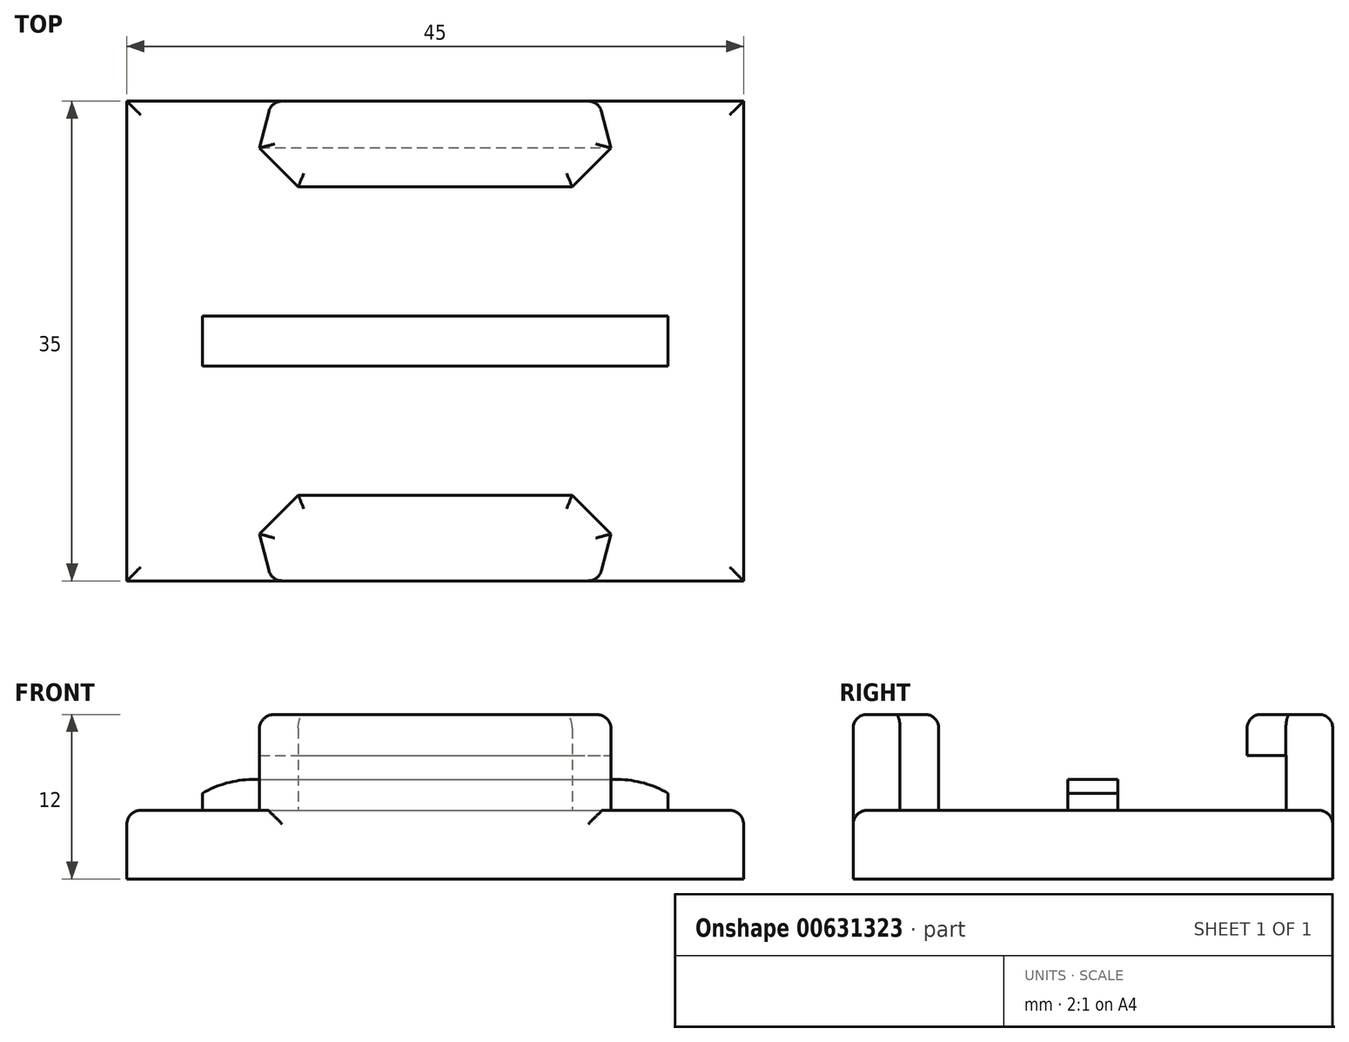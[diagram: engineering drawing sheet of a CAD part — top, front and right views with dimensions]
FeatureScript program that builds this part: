
annotation { "Feature Type Name" : "Feature", "Feature Type Description" : "" }
export const myFeature = defineFeature(function(context is Context, id is Id, definition is map)
    precondition{}
    {
        {
            var Q0;
            Q0=qCreatedBy(makeId("Top.planeOp"),FACE);
            var sketch = newSketch(context, id + "F0", { "sketchPlane" : qUnion([Q0])});
            skLineSegment(sketch, "E0.rect.bottom", {"start": v(-22.5, 17.5) * mm, "end": v(22.5, 17.5) * mm});
            skLineSegment(sketch, "E0.rect.top", {"start": v(-22.5, -17.5) * mm, "end": v(22.5, -17.5) * mm});
            skLineSegment(sketch, "E0.rect.left", {"start": v(-22.5, 17.5) * mm, "end": v(-22.5, -17.5) * mm});
            skLineSegment(sketch, "E0.rect.right", {"start": v(22.5, 17.5) * mm, "end": v(22.5, -17.5) * mm});
            skPoint(sketch, "E0.rect.middle", {"position": v(0, 0) * mm});
            skSolve(sketch);
        }
        {
            var Q0;
            Q0=makeQuery(id+"F0.imprint","IMPRINT",FACE,{"disambiguationData":[TD([[makeQuery(id+"F0.imprint","IMPRINT",EDGE,{"derivedFrom":sQuery(id+"F0.wireOp",EDGE,"E0.rect.bottom")}),-1.0]])]});
            extrude(context, id + "F1", {"entities" : qUnion([Q0]), "depth" : 5 * mm});
        }
        {
            var Q0;
            Q0=makeQuery(id+"F1.opExtrude","CAP_FACE",FACE,{"disambiguationData":[OSD([sQuery(id+"F0.wireOp",EDGE,"E0.rect.bottom"),sQuery(id+"F0.wireOp",EDGE,"E0.rect.top"),sQuery(id+"F0.wireOp",EDGE,"E0.rect.left"),sQuery(id+"F0.wireOp",EDGE,"E0.rect.right")])],"isStart":false});
            var sketch = newSketch(context, id + "F2", { "sketchPlane" : qUnion([Q0])});
            skLineSegment(sketch, "E1.rect.bottom", {"start": v(-17, 1.82) * mm, "end": v(17, 1.82) * mm});
            skLineSegment(sketch, "E1.rect.top", {"start": v(-17, -1.83) * mm, "end": v(17, -1.83) * mm});
            skLineSegment(sketch, "E1.rect.left", {"start": v(-17, 1.82) * mm, "end": v(-17, -1.83) * mm});
            skLineSegment(sketch, "E1.rect.right", {"start": v(17, 1.82) * mm, "end": v(17, -1.83) * mm});
            skPoint(sketch, "E1.rect.middle", {"position": v(0, 0) * mm});
            skSolve(sketch);
        }
        {
            var Q0;
            Q0=makeQuery(id+"F2.imprint","IMPRINT",FACE,{"disambiguationData":[TD([[makeQuery(id+"F2.imprint","IMPRINT",EDGE,{"derivedFrom":sQuery(id+"F2.wireOp",EDGE,"E1.rect.bottom")}),-1.0]])]});
            extrude(context, id + "F3", {"entities" : qUnion([Q0]), "operationType" : NewBodyOperationType.ADD, "depth" : 2.25 * mm});
        }
        {
            var Q0;
            Q0=makeQuery(id+"F3.opExtrude","SWEPT_FACE",FACE,{"disambiguationData":[OSD([sQuery(id+"F2.wireOp",EDGE,"E1.rect.top")])]});
            var sketch = newSketch(context, id + "F4", { "sketchPlane" : qUnion([Q0])});
            skLineSegment(sketch, "E2", {"start": v(-17, 7.25) * mm, "end": v(17, 7.25) * mm, "construction": true});
            skLineSegment(sketch, "E3.0", {"start": v(-17, 6.25) * mm, "end": v(17, 6.25) * mm});
            skArc(sketch, "E4", {"start": v(-13.26, 7.25) * mm, "mid": v(-15.2, 7) * mm, "end": v(-17, 6.25) * mm});
            skLineSegment(sketch, "E5", {"start": v(0, 0) * mm, "end": v(0, 15.47) * mm, "construction": true});
            skArc(sketch, "E6.0.MirrorCS", {"start": v(13.26, 7.25) * mm, "mid": v(15.2, 7) * mm, "end": v(17, 6.25) * mm});
            skLineSegment(sketch, "E7", {"start": v(-17, 6.25) * mm, "end": v(-18.16, 6.25) * mm});
            skLineSegment(sketch, "E8", {"start": v(-18.16, 6.25) * mm, "end": v(-18.16, 8.7) * mm});
            skLineSegment(sketch, "E9", {"start": v(-18.16, 8.7) * mm, "end": v(-13.25, 8.7) * mm});
            skLineSegment(sketch, "E10", {"start": v(-13.25, 8.7) * mm, "end": v(-13.26, 7.25) * mm});
            skLineSegment(sketch, "E11", {"start": v(13.26, 7.25) * mm, "end": v(13.26, 8.4) * mm});
            skLineSegment(sketch, "E12", {"start": v(13.26, 8.4) * mm, "end": v(18.11, 8.4) * mm});
            skLineSegment(sketch, "E13", {"start": v(18.11, 8.4) * mm, "end": v(18.11, 6.28) * mm});
            skLineSegment(sketch, "E14", {"start": v(18.11, 6.28) * mm, "end": v(17, 6.25) * mm});
            skSolve(sketch);
        }
        {
            var Q0;
            {var subQ0=sQuery(id+"F2.wireOp",EDGE,"E1.rect.top");var subQ1=makeQuery(id+"F3.opExtrude","CAP_EDGE",EDGE,{"disambiguationData":[OSD([subQ0])],"isStart":false});var subQ2=sQuery(id+"F4.wireOp",EDGE,"E4");var subQ3=makeQuery(id+"F4.imprint","INTERSECT",VERTEX,{"derivedFrom":[subQ1,subQ2]});var subQ6=makeQuery(id+"F4.imprint","IMPRINT",EDGE,{"disambiguationData":[TD([[subQ3,1.0]])],"derivedFrom":subQ1});var subQ8=sQuery(id+"F4.wireOp",EDGE,"E7");var subQ13=sQuery(id+"F4.wireOp",EDGE,"E6.0.MirrorCS");var subQ18=makeQuery(id+"F4.imprint","INTERSECT",VERTEX,{"derivedFrom":[subQ1,subQ13]});var subQ19=makeQuery(id+"F4.imprint","IMPRINT",EDGE,{"disambiguationData":[TD([[subQ18,-1.0]])],"derivedFrom":subQ1});var subQ20=sQuery(id+"F4.wireOp",EDGE,"E11");Q0=qUnion([makeQuery(id+"F4.imprint","IMPRINT",FACE,{"disambiguationData":[TD([[makeQuery(id+"F4.imprint","IMPRINT",EDGE,{"derivedFrom":subQ8}),-1.0]])]}),makeQuery(id+"F4.imprint","IMPRINT",FACE,{"disambiguationData":[TD([[subQ6,-1.0]])]}),makeQuery(id+"F4.imprint","IMPRINT",FACE,{"disambiguationData":[TD([[makeQuery(id+"F4.imprint","IMPRINT",EDGE,{"derivedFrom":subQ20}),-1.0]])]}),makeQuery(id+"F4.imprint","IMPRINT",FACE,{"disambiguationData":[TD([[subQ19,-1.0]])]})]);}
            extrude(context, id + "F5", {"entities" : qUnion([Q0]), "operationType" : NewBodyOperationType.REMOVE, "flatOperationType" : FlatOperationType.REMOVE, "endBound" : BoundingType.THROUGH_ALL, "oppositeDirection" : true, "depth" : 25 * mm, "offsetDistance" : 25 * mm, "domain" : OperationDomain.MODEL});
        }
        {
            var Q0;
            Q0=makeQuery(id+"F1.opExtrude","CAP_FACE",FACE,{"disambiguationData":[OSD([sQuery(id+"F0.wireOp",EDGE,"E0.rect.bottom"),sQuery(id+"F0.wireOp",EDGE,"E0.rect.top"),sQuery(id+"F0.wireOp",EDGE,"E0.rect.left"),sQuery(id+"F0.wireOp",EDGE,"E0.rect.right")])],"isStart":false});
            var sketch = newSketch(context, id + "F6", { "sketchPlane" : qUnion([Q0])});
            skLineSegment(sketch, "E15.rect.bottom", {"start": v(-11.94, 17.5) * mm, "end": v(11.94, 17.5) * mm, "construction": true});
            skPoint(sketch, "E15.rect.middle", {"position": v(0, 0) * mm});
            skLineSegment(sketch, "E16.0", {"start": v(-10, 11.25) * mm, "end": v(10, 11.25) * mm});
            skLineSegment(sketch, "E17", {"start": v(-10, 11.25) * mm, "end": v(-12.82, 14.08) * mm, "construction": true});
            skLineSegment(sketch, "E18.0.MirrorCS", {"start": v(10, 11.25) * mm, "end": v(12.82, 14.08) * mm, "construction": true});
            skLineSegment(sketch, "E19", {"start": v(10, 11.25) * mm, "end": v(12.82, 14.08) * mm});
            skLineSegment(sketch, "E20", {"start": v(11.94, 17.5) * mm, "end": v(-11.94, 17.5) * mm});
            skLineSegment(sketch, "E21", {"start": v(-12.82, 14.08) * mm, "end": v(-10, 11.25) * mm});
            skLineSegment(sketch, "E22.0.MirrorCS", {"start": v(-10, -11.25) * mm, "end": v(-12.82, -14.08) * mm, "construction": true});
            skLineSegment(sketch, "E22.1.MirrorCS", {"start": v(-11.94, -17.5) * mm, "end": v(11.94, -17.5) * mm, "construction": true});
            skLineSegment(sketch, "E22.2.MirrorCS", {"start": v(-11.94, -17.5) * mm, "end": v(11.94, -17.5) * mm, "construction": true});
            skLineSegment(sketch, "E22.4.MirrorCS", {"start": v(-10, -11.25) * mm, "end": v(-12.82, -14.08) * mm, "construction": true});
            skLineSegment(sketch, "E22.5.MirrorCS", {"start": v(10, -11.25) * mm, "end": v(12.82, -14.08) * mm, "construction": true});
            skLineSegment(sketch, "E22.7.MirrorCS", {"start": v(11.94, -17.5) * mm, "end": v(-11.94, -17.5) * mm});
            skLineSegment(sketch, "E22.9.MirrorCS", {"start": v(10, -11.25) * mm, "end": v(12.82, -14.08) * mm});
            skLineSegment(sketch, "E22.10.MirrorCS", {"start": v(-12.82, -14.08) * mm, "end": v(-10, -11.25) * mm});
            skLineSegment(sketch, "E22.12.MirrorCS", {"start": v(-10, -11.25) * mm, "end": v(10, -11.25) * mm});
            skLineSegment(sketch, "E23", {"start": v(12.82, 14.08) * mm, "end": v(11.94, 17.5) * mm});
            skLineSegment(sketch, "E24.0.MirrorCS", {"start": v(12.82, -14.08) * mm, "end": v(11.94, -17.5) * mm});
            skLineSegment(sketch, "E25.0.MirrorCS", {"start": v(-12.82, 14.08) * mm, "end": v(-11.94, 17.5) * mm});
            skLineSegment(sketch, "E26.0.MirrorCS", {"start": v(-12.82, -14.08) * mm, "end": v(-11.94, -17.5) * mm});
            skSolve(sketch);
        }
        {
            var Q0;
            {Q0=qUnion([makeQuery(id+"F6.imprint","IMPRINT",FACE,{"disambiguationData":[TD([[makeQuery(id+"F6.imprint","IMPRINT",EDGE,{"derivedFrom":sQuery(id+"F6.wireOp",EDGE,"E16.0")}),1.0]])]}),makeQuery(id+"F6.imprint","IMPRINT",FACE,{"disambiguationData":[TD([[makeQuery(id+"F6.imprint","IMPRINT",EDGE,{"derivedFrom":sQuery(id+"F6.wireOp",EDGE,"E22.7.MirrorCS")}),1.0]])]})]);}
            extrude(context, id + "F7", {"entities" : qUnion([Q0]), "operationType" : NewBodyOperationType.ADD, "flatOperationType" : FlatOperationType.REMOVE, "depth" : 7 * mm, "offsetDistance" : 25 * mm, "domain" : OperationDomain.MODEL});
        }
        {
            var Q0;
            Q0=qCreatedBy(makeId("Right.planeOp"),FACE);
            var sketch = newSketch(context, id + "F8", { "sketchPlane" : qUnion([Q0])});
            skLineSegment(sketch, "E27.0", {"start": v(14.1, 9) * mm, "end": v(14.1, 5) * mm});
            skLineSegment(sketch, "E28.bottom", {"start": v(14.1, 5) * mm, "end": v(10.15, 5) * mm});
            skLineSegment(sketch, "E28.top", {"start": v(14.1, 9) * mm, "end": v(10.15, 9) * mm});
            skLineSegment(sketch, "E28.left", {"start": v(14.1, 5) * mm, "end": v(14.1, 9) * mm});
            skLineSegment(sketch, "E28.right", {"start": v(10.15, 5) * mm, "end": v(10.15, 9) * mm});
            skLineSegment(sketch, "E29.0.MirrorCS", {"start": v(-14.1, 5) * mm, "end": v(-14.1, 9) * mm});
            skLineSegment(sketch, "E29.1.MirrorCS", {"start": v(-14.1, 9) * mm, "end": v(-14.1, 5) * mm});
            skLineSegment(sketch, "E29.2.MirrorCS", {"start": v(-14.1, 9) * mm, "end": v(-10.15, 9) * mm});
            skLineSegment(sketch, "E29.3.MirrorCS", {"start": v(-10.15, 5) * mm, "end": v(-10.15, 9) * mm});
            skLineSegment(sketch, "E29.4.MirrorCS", {"start": v(-14.1, 5) * mm, "end": v(-10.15, 5) * mm});
            skSolve(sketch);
        }
        {
            var Q0;
            {Q0=qUnion([makeQuery(id+"F8.imprint","IMPRINT",FACE,{"disambiguationData":[TD([[makeQuery(id+"F8.imprint","IMPRINT",EDGE,{"derivedFrom":sQuery(id+"F8.wireOp",EDGE,"E28.bottom")}),-1.0]])]}),makeQuery(id+"F8.imprint","IMPRINT",FACE,{"disambiguationData":[TD([[makeQuery(id+"F8.imprint","IMPRINT",EDGE,{"derivedFrom":sQuery(id+"F8.wireOp",EDGE,"E29.1.MirrorCS")}),1.0]])]})]);}
            extrude(context, id + "F9", {"entities" : qUnion([Q0]), "operationType" : NewBodyOperationType.REMOVE, "endBound" : BoundingType.SYMMETRIC, "oppositeDirection" : true, "depth" : 31.01 * mm});
        }
        {
            var Q0;
            Q0=makeQuery(id+"F7.opExtrude","CAP_FACE",FACE,{"disambiguationData":[OSD([sQuery(id+"F6.wireOp",EDGE,"E16.0"),sQuery(id+"F6.wireOp",EDGE,"E19"),sQuery(id+"F6.wireOp",EDGE,"E20"),sQuery(id+"F6.wireOp",EDGE,"E21"),sQuery(id+"F6.wireOp",EDGE,"E23"),sQuery(id+"F6.wireOp",EDGE,"E25.0.MirrorCS")])],"isStart":false});
            var Q1;
            Q1=makeQuery(id+"F7.opExtrude","CAP_FACE",FACE,{"disambiguationData":[OSD([sQuery(id+"F6.wireOp",EDGE,"E22.7.MirrorCS"),sQuery(id+"F6.wireOp",EDGE,"E22.9.MirrorCS"),sQuery(id+"F6.wireOp",EDGE,"E22.10.MirrorCS"),sQuery(id+"F6.wireOp",EDGE,"E22.12.MirrorCS"),sQuery(id+"F6.wireOp",EDGE,"E24.0.MirrorCS"),sQuery(id+"F6.wireOp",EDGE,"E26.0.MirrorCS")])],"isStart":false});
            var Q2;
            Q2=makeQuery(id+"F7.opExtrude","SWEPT_EDGE",EDGE,{"disambiguationData":[OSD([sQuery(id+"F0.wireOp",EDGE,"E0.rect.bottom"),sQuery(id+"F6.wireOp",EDGE,"E20"),sQuery(id+"F6.wireOp",EDGE,"E23")])]});
            var Q3;
            Q3=makeQuery(id+"F7.opExtrude","SWEPT_EDGE",EDGE,{"disambiguationData":[OSD([sQuery(id+"F0.wireOp",EDGE,"E0.rect.bottom"),sQuery(id+"F6.wireOp",EDGE,"E20"),sQuery(id+"F6.wireOp",EDGE,"E25.0.MirrorCS")])]});
            var Q4;
            Q4=makeQuery(id+"F7.opExtrude","SWEPT_EDGE",EDGE,{"disambiguationData":[OSD([sQuery(id+"F0.wireOp",EDGE,"E0.rect.top"),sQuery(id+"F6.wireOp",EDGE,"E22.7.MirrorCS"),sQuery(id+"F6.wireOp",EDGE,"E24.0.MirrorCS")])]});
            var Q5;
            Q5=makeQuery(id+"F7.opExtrude","SWEPT_EDGE",EDGE,{"disambiguationData":[OSD([sQuery(id+"F0.wireOp",EDGE,"E0.rect.top"),sQuery(id+"F6.wireOp",EDGE,"E22.7.MirrorCS"),sQuery(id+"F6.wireOp",EDGE,"E26.0.MirrorCS")])]});
            fillet(context, id + "F10", {"entities" : qUnion([Q0, Q1, Q2, Q3, Q4, Q5]), "radius" : 1 * mm, "tangentPropagation" : true, "allowEdgeOverflow" : false});
        }
        {
            var Q0;
            {var subQ0=sQuery(id+"F0.wireOp",EDGE,"E0.rect.top");var subQ1=sQuery(id+"F0.wireOp",EDGE,"E0.rect.right");Q0=makeQuery(id+"F7.boolean.opBoolean","SPLIT",EDGE,{"disambiguationData":[TD([makeQuery(id+"F1.opExtrude","SWEPT_FACE",FACE,{"disambiguationData":[OSD([subQ1])]})])],"derivedFrom":makeQuery(id+"F1.opExtrude","CAP_EDGE",EDGE,{"disambiguationData":[OSD([subQ0])],"isStart":false})});}
            var Q1;
            Q1=makeQuery(id+"F1.opExtrude","CAP_EDGE",EDGE,{"disambiguationData":[OSD([sQuery(id+"F0.wireOp",EDGE,"E0.rect.right")])],"isStart":false});
            var Q2;
            {var subQ0=sQuery(id+"F0.wireOp",EDGE,"E0.rect.bottom");var subQ1=sQuery(id+"F0.wireOp",EDGE,"E0.rect.right");Q2=makeQuery(id+"F7.boolean.opBoolean","SPLIT",EDGE,{"disambiguationData":[TD([makeQuery(id+"F1.opExtrude","SWEPT_FACE",FACE,{"disambiguationData":[OSD([subQ1])]})])],"derivedFrom":makeQuery(id+"F1.opExtrude","CAP_EDGE",EDGE,{"disambiguationData":[OSD([subQ0])],"isStart":false})});}
            var Q3;
            {var subQ0=sQuery(id+"F0.wireOp",EDGE,"E0.rect.bottom");var subQ1=sQuery(id+"F0.wireOp",EDGE,"E0.rect.left");Q3=makeQuery(id+"F7.boolean.opBoolean","SPLIT",EDGE,{"disambiguationData":[TD([makeQuery(id+"F1.opExtrude","SWEPT_FACE",FACE,{"disambiguationData":[OSD([subQ1])]})])],"derivedFrom":makeQuery(id+"F1.opExtrude","CAP_EDGE",EDGE,{"disambiguationData":[OSD([subQ0])],"isStart":false})});}
            var Q4;
            Q4=makeQuery(id+"F1.opExtrude","CAP_EDGE",EDGE,{"disambiguationData":[OSD([sQuery(id+"F0.wireOp",EDGE,"E0.rect.left")])],"isStart":false});
            var Q5;
            {var subQ0=sQuery(id+"F0.wireOp",EDGE,"E0.rect.top");var subQ1=sQuery(id+"F0.wireOp",EDGE,"E0.rect.left");Q5=makeQuery(id+"F7.boolean.opBoolean","SPLIT",EDGE,{"disambiguationData":[TD([makeQuery(id+"F1.opExtrude","SWEPT_FACE",FACE,{"disambiguationData":[OSD([subQ1])]})])],"derivedFrom":makeQuery(id+"F1.opExtrude","CAP_EDGE",EDGE,{"disambiguationData":[OSD([subQ0])],"isStart":false})});}
            fillet(context, id + "F11", {"entities" : qUnion([Q0, Q1, Q2, Q3, Q4, Q5]), "radius" : 1 * mm, "allowEdgeOverflow" : false});
        }
    });
